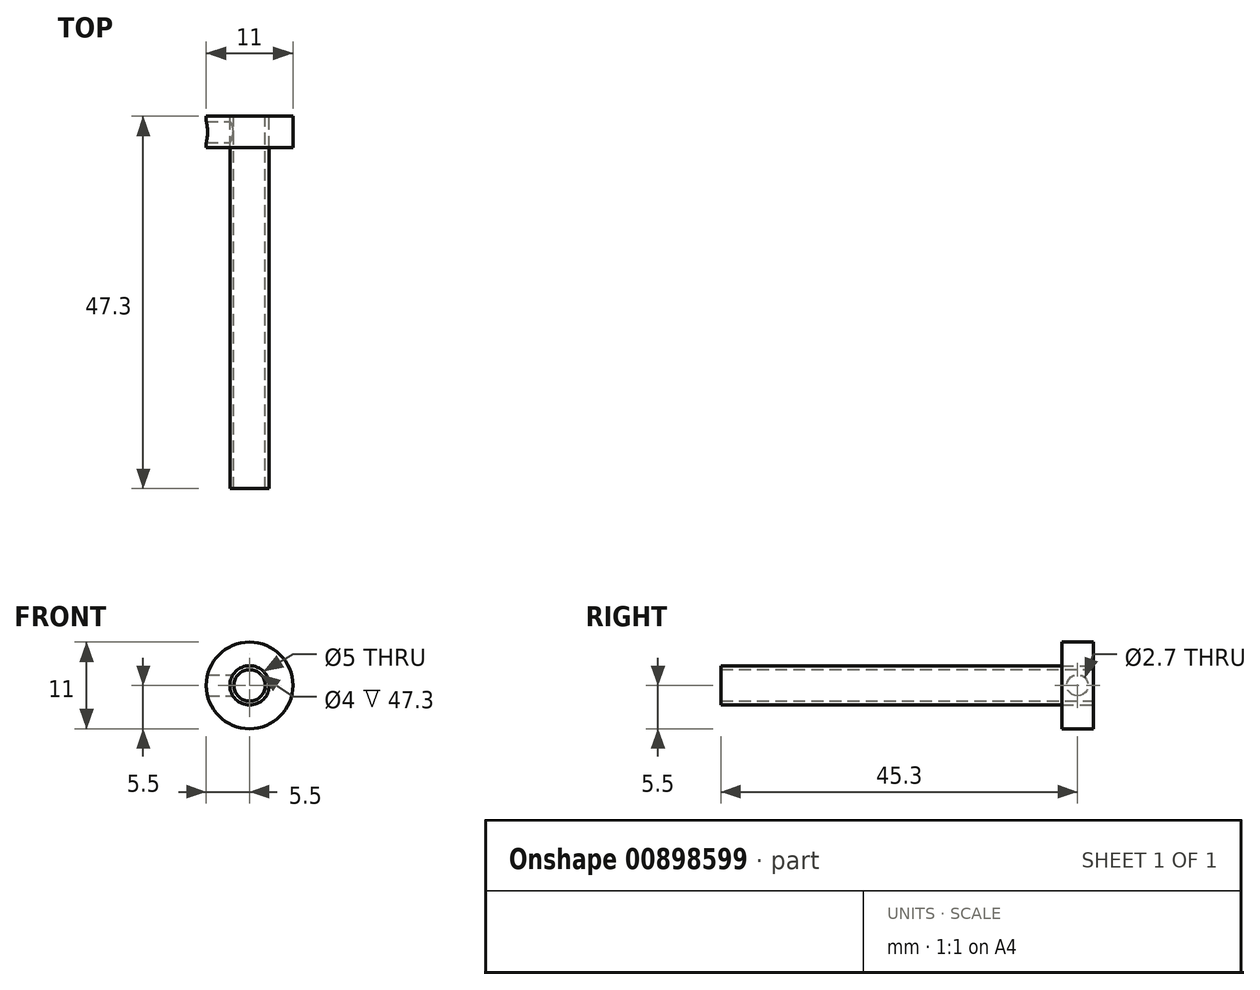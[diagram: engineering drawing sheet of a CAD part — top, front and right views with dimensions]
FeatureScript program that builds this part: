
annotation { "Feature Type Name" : "Feature", "Feature Type Description" : "" }
export const myFeature = defineFeature(function(context is Context, id is Id, definition is map)
    precondition{}
    {
        {
            var Q0;
            Q0=qCreatedBy(makeId("Front.planeOp"),FACE);
            var sketch = newSketch(context, id + "F0", { "sketchPlane" : qUnion([Q0])});
            skCircle(sketch, "E0", {"center": v(0, 0) * mm, "radius": 2 * mm});
            skCircle(sketch, "E1", {"center": v(0, 0) * mm, "radius": 2.5 * mm});
            skSolve(sketch);
        }
        {
            var Q0;
            Q0=qSketchRegion(id+"F0",true);
            extrude(context, id + "F1", {"entities" : qUnion([Q0]), "depth" : 47.3 * mm});
        }
        {
            var Q0;
            Q0=qCreatedBy(makeId("Front.planeOp"),FACE);
            var sketch = newSketch(context, id + "F2", { "sketchPlane" : qUnion([Q0])});
            skCircle(sketch, "E2", {"center": v(0, 0) * mm, "radius": 2.5 * mm});
            skCircle(sketch, "E3", {"center": v(0, 0) * mm, "radius": 5.5 * mm});
            skSolve(sketch);
        }
        {
            var Q0;
            Q0=qSketchRegion(id+"F2",true);
            extrude(context, id + "F3", {"entities" : qUnion([Q0]), "depth" : 4 * mm});
        }
        {
            var Q0;
            Q0=qCreatedBy(makeId("Right.planeOp"),FACE);
            var sketch = newSketch(context, id + "F4", { "sketchPlane" : qUnion([Q0])});
            skLineSegment(sketch, "E4", {"start": v(-4, 5.5) * mm, "end": v(0, 5.5) * mm, "construction": true});
            skLineSegment(sketch, "E5", {"start": v(-2, 5.5) * mm, "end": v(-2, -9.05) * mm, "construction": true});
            skCircle(sketch, "E6", {"center": v(-2, 0) * mm, "radius": 1.38 * mm});
            skSolve(sketch);
        }
        {
            var Q0;
            Q0=sQuery(id+"F4.wireOp",VERTEX,"E6.center");
            var Q1;
            Q1=makeQuery(id+"F3.opExtrude","SWEPT_BODY",BODY,{"disambiguationData":[OSD([sQuery(id+"F2.wireOp",EDGE,"E2"),sQuery(id+"F2.wireOp",EDGE,"E3")])]});
            hole(context, id + "F5", {"style" : HoleStyle.SIMPLE, "holeDiameter" : 2.7 * mm, "endStyle" : HoleEndStyle.THROUGH, "locations" : qUnion([Q0]), "scope" : qUnion([Q1])});
        }
    });
